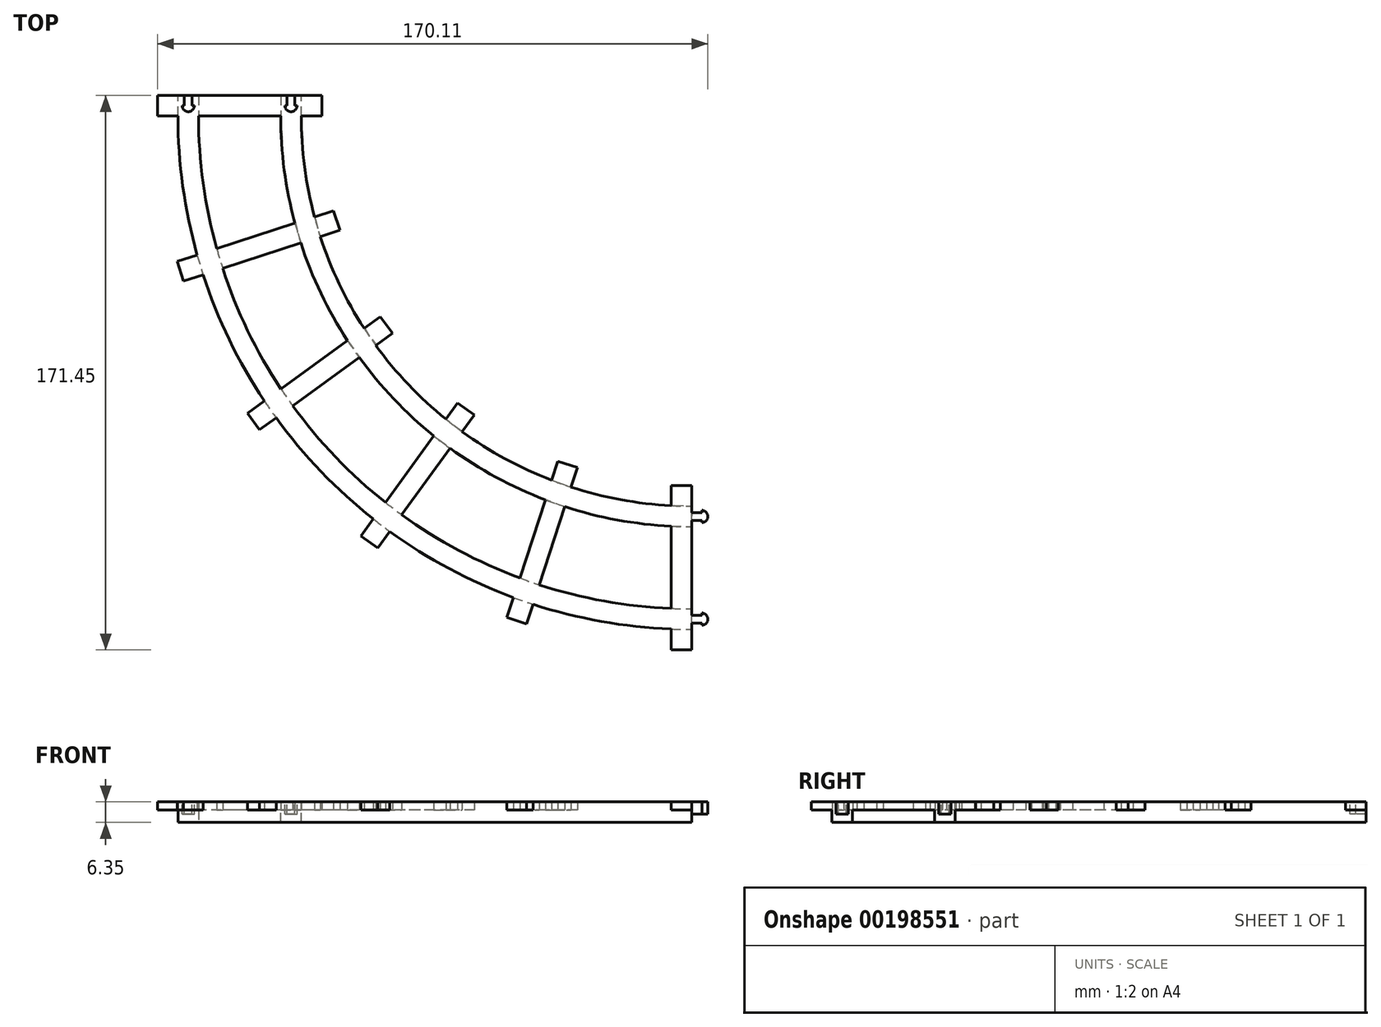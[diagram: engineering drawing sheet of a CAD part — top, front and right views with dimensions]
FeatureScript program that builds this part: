
annotation { "Feature Type Name" : "Feature", "Feature Type Description" : "" }
export const myFeature = defineFeature(function(context is Context, id is Id, definition is map)
    precondition{}
    {
        {
            var Q0;
            Q0=qCreatedBy(makeId("Top.planeOp"),FACE);
            var sketch = newSketch(context, id + "F0", { "sketchPlane" : qUnion([Q0])});
            skLineSegment(sketch, "E0.bottom", {"start": v(76.2, 76.2) * mm, "end": v(-76.2, 76.2) * mm, "construction": true});
            skPoint(sketch, "E0.middle", {"position": v(0, 0) * mm});
            skLineSegment(sketch, "E1", {"start": v(-76.2, 76.2) * mm, "end": v(-76.2, 101.6) * mm, "construction": true});
            skLineSegment(sketch, "E2", {"start": v(76.2, -76.2) * mm, "end": v(101.6, -76.2) * mm, "construction": true});
            skArc(sketch, "E3", {"start": v(76.2, -76.2) * mm, "mid": v(-31.56, -31.56) * mm, "end": v(-76.2, 76.2) * mm});
            skLineSegment(sketch, "E4", {"start": v(-76.2, 76.2) * mm, "end": v(-50.8, 76.2) * mm, "construction": true});
            skLineSegment(sketch, "E5", {"start": v(-50.8, 76.2) * mm, "end": v(-50.8, 101.6) * mm, "construction": true});
            skLineSegment(sketch, "E6", {"start": v(76.2, -76.2) * mm, "end": v(76.2, -50.8) * mm, "construction": true});
            skLineSegment(sketch, "E7", {"start": v(76.2, -50.8) * mm, "end": v(101.6, -50.8) * mm, "construction": true});
            skArc(sketch, "E8", {"start": v(76.2, -50.8) * mm, "mid": v(-13.6, -13.6) * mm, "end": v(-50.8, 76.2) * mm});
            skLineSegment(sketch, "E9", {"start": v(-76.2, 76.2) * mm, "end": v(-82.55, 76.2) * mm, "construction": true});
            skLineSegment(sketch, "E10", {"start": v(76.2, -76.2) * mm, "end": v(76.2, -82.55) * mm, "construction": true});
            skLineSegment(sketch, "E11", {"start": v(76.2, -82.55) * mm, "end": v(101.6, -82.55) * mm, "construction": true});
            skArc(sketch, "E12", {"start": v(76.2, -82.55) * mm, "mid": v(-36.05, -36.05) * mm, "end": v(-82.55, 76.2) * mm});
            skLineSegment(sketch, "E13", {"start": v(-82.55, 76.2) * mm, "end": v(-76.2, 76.2) * mm});
            skLineSegment(sketch, "E14", {"start": v(76.2, -82.55) * mm, "end": v(76.2, -76.2) * mm});
            skLineSegment(sketch, "E15", {"start": v(-50.8, 76.2) * mm, "end": v(-44.45, 76.2) * mm});
            skLineSegment(sketch, "E16", {"start": v(-44.45, 76.2) * mm, "end": v(-44.45, 101.6) * mm, "construction": true});
            skLineSegment(sketch, "E17", {"start": v(76.2, -44.45) * mm, "end": v(101.6, -44.45) * mm, "construction": true});
            skArc(sketch, "E18", {"start": v(76.2, -44.45) * mm, "mid": v(-9.11, -9.11) * mm, "end": v(-44.45, 76.2) * mm});
            skLineSegment(sketch, "E19", {"start": v(76.2, -44.45) * mm, "end": v(76.2, -50.8) * mm});
            skSolve(sketch);
        }
        {
            var Q0;
            Q0=qSketchRegion(id+"F0",true);
            extrude(context, id + "F1", {"entities" : qUnion([Q0]), "depth" : 6.35 * mm});
        }
        {
            var Q0;
            Q0=qCreatedBy(makeId("Top.planeOp"),FACE);
            var sketch = newSketch(context, id + "F2", { "sketchPlane" : qUnion([Q0])});
            skLineSegment(sketch, "E20.bottom", {"start": v(76.2, 76.2) * mm, "end": v(-76.2, 76.2) * mm, "construction": true});
            skLineSegment(sketch, "E20.top", {"start": v(76.2, -76.2) * mm, "end": v(-76.2, -76.2) * mm, "construction": true});
            skLineSegment(sketch, "E20.right", {"start": v(-76.2, 76.2) * mm, "end": v(-76.2, -76.2) * mm, "construction": true});
            skPoint(sketch, "E20.middle", {"position": v(0, 0) * mm});
            skLineSegment(sketch, "E21", {"start": v(76.2, -76.2) * mm, "end": v(76.2, -88.9) * mm, "construction": true});
            skLineSegment(sketch, "E22", {"start": v(76.2, -76.2) * mm, "end": v(76.2, -38.1) * mm, "construction": true});
            skLineSegment(sketch, "E23", {"start": v(76.2, -38.1) * mm, "end": v(69.85, -38.1) * mm});
            skLineSegment(sketch, "E24", {"start": v(76.2, -88.9) * mm, "end": v(69.85, -88.9) * mm});
            skLineSegment(sketch, "E25", {"start": v(69.85, -38.1) * mm, "end": v(69.85, -88.9) * mm});
            skLineSegment(sketch, "E26", {"start": v(76.2, -38.1) * mm, "end": v(76.2, -88.9) * mm});
            skArc(sketch, "E27.0", {"start": v(76.2, -44.45) * mm, "mid": v(-9.11, -9.11) * mm, "end": v(-44.45, 76.2) * mm, "construction": true});
            skLineSegment(sketch, "E28.1.0", {"start": v(40.88, -32.5) * mm, "end": v(25.18, -80.82) * mm});
            skLineSegment(sketch, "E28.1.1", {"start": v(34.84, -30.54) * mm, "end": v(19.14, -78.86) * mm});
            skLineSegment(sketch, "E28.1.2", {"start": v(40.88, -32.5) * mm, "end": v(34.84, -30.54) * mm});
            skLineSegment(sketch, "E28.1.3", {"start": v(25.18, -80.82) * mm, "end": v(19.14, -78.86) * mm});
            skLineSegment(sketch, "E28.2.0", {"start": v(9.02, -16.27) * mm, "end": v(-20.84, -57.37) * mm});
            skLineSegment(sketch, "E28.2.1", {"start": v(3.88, -12.54) * mm, "end": v(-25.98, -53.64) * mm});
            skLineSegment(sketch, "E28.2.2", {"start": v(9.02, -16.27) * mm, "end": v(3.88, -12.54) * mm});
            skLineSegment(sketch, "E28.2.3", {"start": v(-20.84, -57.37) * mm, "end": v(-25.98, -53.64) * mm});
            skLineSegment(sketch, "E28.3.0", {"start": v(-16.27, 9.02) * mm, "end": v(-57.37, -20.84) * mm});
            skLineSegment(sketch, "E28.3.1", {"start": v(-20, 14.15) * mm, "end": v(-61.1, -15.7) * mm});
            skLineSegment(sketch, "E28.3.2", {"start": v(-16.27, 9.02) * mm, "end": v(-20, 14.15) * mm});
            skLineSegment(sketch, "E28.3.3", {"start": v(-57.37, -20.84) * mm, "end": v(-61.1, -15.7) * mm});
            skLineSegment(sketch, "E28.4.0", {"start": v(-32.5, 40.88) * mm, "end": v(-80.82, 25.18) * mm});
            skLineSegment(sketch, "E28.4.1", {"start": v(-34.47, 46.92) * mm, "end": v(-82.78, 31.22) * mm});
            skLineSegment(sketch, "E28.4.2", {"start": v(-32.5, 40.88) * mm, "end": v(-34.47, 46.92) * mm});
            skLineSegment(sketch, "E28.4.3", {"start": v(-80.82, 25.18) * mm, "end": v(-82.78, 31.22) * mm});
            skLineSegment(sketch, "E28.5.0", {"start": v(-38.1, 76.2) * mm, "end": v(-88.9, 76.2) * mm});
            skLineSegment(sketch, "E28.5.1", {"start": v(-38.1, 82.55) * mm, "end": v(-88.9, 82.55) * mm});
            skLineSegment(sketch, "E28.5.2", {"start": v(-38.1, 76.2) * mm, "end": v(-38.1, 82.55) * mm});
            skLineSegment(sketch, "E28.5.3", {"start": v(-88.9, 76.2) * mm, "end": v(-88.9, 82.55) * mm});
            skLineSegment(sketch, "E28.anchor1", {"start": v(76.2, 76.2) * mm, "end": v(76.2, -88.9) * mm, "construction": true});
            skLineSegment(sketch, "E28.anchor2", {"start": v(76.2, 76.2) * mm, "end": v(-88.9, 76.2) * mm, "construction": true});
            skSolve(sketch);
        }
        {
            var Q0;
            Q0 = qSketchRegion(id + "F2", true);
            extrude(context, id + "F3", {"entities" : qUnion([Q0]), "operationType" : NewBodyOperationType.ADD, "depth" : 6.35 * mm, "hasSecondDirection" : true, "secondDirectionOppositeDirection" : false, "secondDirectionDepth" : 3.8 * mm});
        }
        {
            var Q0;
            Q0=makeQuery(id+"F3.opExtrude","CAP_FACE",FACE,{"disambiguationData":[OSD([sQuery(id+"F2.wireOp",EDGE,"E28.5.0"),sQuery(id+"F2.wireOp",EDGE,"E28.5.1"),sQuery(id+"F2.wireOp",EDGE,"E28.5.2"),sQuery(id+"F2.wireOp",EDGE,"E28.5.3")])],"isStart":true});
            var sketch = newSketch(context, id + "F4", { "sketchPlane" : qUnion([Q0])});
            skArc(sketch, "E29.0", {"start": v(76.2, 44.45) * mm, "mid": v(-9.11, 9.11) * mm, "end": v(-44.45, -76.2) * mm});
            skArc(sketch, "E30.0", {"start": v(76.2, 82.55) * mm, "mid": v(-36.05, 36.05) * mm, "end": v(-82.55, -76.2) * mm});
            skLineSegment(sketch, "E31", {"start": v(-82.55, -76.2) * mm, "end": v(-82.55, -82.55) * mm});
            skLineSegment(sketch, "E32", {"start": v(-44.45, -76.2) * mm, "end": v(-44.45, -82.55) * mm});
            skLineSegment(sketch, "E33", {"start": v(-44.45, -82.55) * mm, "end": v(-50.8, -82.55) * mm});
            skPoint(sketch, "E33.endSnap0", {"position": v(-63.5, -82.55) * mm});
            skLineSegment(sketch, "E34", {"start": v(-82.55, -82.55) * mm, "end": v(-76.2, -82.55) * mm});
            skLineSegment(sketch, "E35", {"start": v(-50.8, -82.55) * mm, "end": v(-50.8, -76.2) * mm});
            skLineSegment(sketch, "E36", {"start": v(-50.8, -76.2) * mm, "end": v(-44.45, -76.2) * mm});
            skLineSegment(sketch, "E37", {"start": v(-76.2, -82.55) * mm, "end": v(-76.2, -76.2) * mm});
            skLineSegment(sketch, "E38", {"start": v(-76.2, -76.2) * mm, "end": v(-82.55, -76.2) * mm});
            skSolve(sketch);
        }
        {
            var Q0;
            Q0 = qSketchRegion(id + "F4", true);
            var Q1;
            Q1=makeQuery(id+"F1.opExtrude","CAP_FACE",FACE,{"disambiguationData":[OSD([sQuery(id+"F0.wireOp",EDGE,"E8"),sQuery(id+"F0.wireOp",EDGE,"E15"),sQuery(id+"F0.wireOp",EDGE,"E18"),sQuery(id+"F0.wireOp",EDGE,"E19")])],"isStart":true});
            extrude(context, id + "F5", {"entities" : qUnion([Q0]), "operationType" : NewBodyOperationType.ADD, "endBound" : BoundingType.UP_TO_SURFACE, "endBoundEntityFace" : qUnion([Q1]), "depth" : 25.4 * mm});
        }
        {
            var Q0;
            Q0=makeQuery(id+"F3.boolean.opBoolean","MERGE",FACE,{"derivedFrom":[makeQuery(id+"F1.opExtrude","CAP_FACE",FACE,{"disambiguationData":[OSD([sQuery(id+"F0.wireOp",EDGE,"E3"),sQuery(id+"F0.wireOp",EDGE,"E12"),sQuery(id+"F0.wireOp",EDGE,"E13"),sQuery(id+"F0.wireOp",EDGE,"E14")])],"isStart":false}),makeQuery(id+"F1.opExtrude","CAP_FACE",FACE,{"disambiguationData":[OSD([sQuery(id+"F0.wireOp",EDGE,"E8"),sQuery(id+"F0.wireOp",EDGE,"E15"),sQuery(id+"F0.wireOp",EDGE,"E18"),sQuery(id+"F0.wireOp",EDGE,"E19")])],"isStart":false}),makeQuery(id+"F3.opExtrude","CAP_FACE",FACE,{"disambiguationData":[OSD([sQuery(id+"F2.wireOp",EDGE,"E23"),sQuery(id+"F2.wireOp",EDGE,"E24"),sQuery(id+"F2.wireOp",EDGE,"E25"),sQuery(id+"F2.wireOp",EDGE,"E26")])],"isStart":false}),makeQuery(id+"F3.opExtrude","CAP_FACE",FACE,{"disambiguationData":[OSD([sQuery(id+"F2.wireOp",EDGE,"E28.1.0"),sQuery(id+"F2.wireOp",EDGE,"E28.1.1"),sQuery(id+"F2.wireOp",EDGE,"E28.1.2"),sQuery(id+"F2.wireOp",EDGE,"E28.1.3")])],"isStart":false}),makeQuery(id+"F3.opExtrude","CAP_FACE",FACE,{"disambiguationData":[OSD([sQuery(id+"F2.wireOp",EDGE,"E28.2.0"),sQuery(id+"F2.wireOp",EDGE,"E28.2.1"),sQuery(id+"F2.wireOp",EDGE,"E28.2.2"),sQuery(id+"F2.wireOp",EDGE,"E28.2.3")])],"isStart":false}),makeQuery(id+"F3.opExtrude","CAP_FACE",FACE,{"disambiguationData":[OSD([sQuery(id+"F2.wireOp",EDGE,"E28.3.0"),sQuery(id+"F2.wireOp",EDGE,"E28.3.1"),sQuery(id+"F2.wireOp",EDGE,"E28.3.2"),sQuery(id+"F2.wireOp",EDGE,"E28.3.3")])],"isStart":false}),makeQuery(id+"F3.opExtrude","CAP_FACE",FACE,{"disambiguationData":[OSD([sQuery(id+"F2.wireOp",EDGE,"E28.4.0"),sQuery(id+"F2.wireOp",EDGE,"E28.4.1"),sQuery(id+"F2.wireOp",EDGE,"E28.4.2"),sQuery(id+"F2.wireOp",EDGE,"E28.4.3")])],"isStart":false}),makeQuery(id+"F3.opExtrude","CAP_FACE",FACE,{"disambiguationData":[OSD([sQuery(id+"F2.wireOp",EDGE,"E28.5.0"),sQuery(id+"F2.wireOp",EDGE,"E28.5.1"),sQuery(id+"F2.wireOp",EDGE,"E28.5.2"),sQuery(id+"F2.wireOp",EDGE,"E28.5.3")])],"isStart":false})]});
            var sketch = newSketch(context, id + "F6", { "sketchPlane" : qUnion([Q0])});
            skLineSegment(sketch, "E39", {"start": v(76.2, -47.62) * mm, "end": v(79.38, -47.62) * mm, "construction": true});
            skLineSegment(sketch, "E40", {"start": v(76.2, -47.62) * mm, "end": v(76.2, -46.43) * mm});
            skLineSegment(sketch, "E41.MirrorCS", {"start": v(76.2, -47.62) * mm, "end": v(76.2, -48.81) * mm});
            skLineSegment(sketch, "E42", {"start": v(76.2, -46.43) * mm, "end": v(79.38, -46.43) * mm});
            skLineSegment(sketch, "E43", {"start": v(79.38, -46.43) * mm, "end": v(79.38, -45.72) * mm});
            skLineSegment(sketch, "E44.MirrorCS", {"start": v(76.2, -48.81) * mm, "end": v(79.38, -48.81) * mm});
            skLineSegment(sketch, "E45.MirrorCS", {"start": v(79.38, -48.81) * mm, "end": v(79.38, -49.53) * mm});
            skArc(sketch, "E46", {"start": v(79.37, -49.53) * mm, "mid": v(81.21, -47.62) * mm, "end": v(79.37, -45.72) * mm});
            skLineSegment(sketch, "E47", {"start": v(76.2, -38.1) * mm, "end": v(76.2, -46.43) * mm, "construction": true});
            skLineSegment(sketch, "E48", {"start": v(76.2, -38.1) * mm, "end": v(76.2, -88.9) * mm, "construction": true});
            skPoint(sketch, "E49", {"position": v(76.2, -63.5) * mm});
            skLineSegment(sketch, "E50", {"start": v(76.2, -63.5) * mm, "end": v(127.23, -63.5) * mm, "construction": true});
            skLineSegment(sketch, "E51.MirrorCS", {"start": v(76.2, -79.38) * mm, "end": v(76.2, -80.57) * mm});
            skLineSegment(sketch, "E52.MirrorCS", {"start": v(76.2, -80.57) * mm, "end": v(79.38, -80.57) * mm});
            skLineSegment(sketch, "E53.MirrorCS", {"start": v(79.38, -80.57) * mm, "end": v(79.38, -81.28) * mm});
            skArc(sketch, "E54.MirrorCS", {"start": v(79.37, -77.47) * mm, "mid": v(81.21, -79.38) * mm, "end": v(79.37, -81.28) * mm});
            skLineSegment(sketch, "E55.MirrorCS", {"start": v(76.2, -79.38) * mm, "end": v(76.2, -78.19) * mm});
            skLineSegment(sketch, "E56.MirrorCS", {"start": v(76.2, -78.19) * mm, "end": v(79.38, -78.19) * mm});
            skLineSegment(sketch, "E57", {"start": v(79.38, -77.47) * mm, "end": v(79.38, -78.19) * mm});
            skSolve(sketch);
        }
        {
            var Q0;
            Q0 = qSketchRegion(id + "F6", true);
            extrude(context, id + "F7", {"entities" : qUnion([Q0]), "operationType" : NewBodyOperationType.ADD, "oppositeDirection" : true, "depth" : 3.8 * mm});
        }
        {
            var Q0;
            Q0=makeQuery(id+"F7.boolean.opBoolean","MERGE",FACE,{"derivedFrom":[makeQuery(id+"F3.boolean.opBoolean","MERGE",FACE,{"derivedFrom":[makeQuery(id+"F1.opExtrude","CAP_FACE",FACE,{"disambiguationData":[OSD([sQuery(id+"F0.wireOp",EDGE,"E3"),sQuery(id+"F0.wireOp",EDGE,"E12"),sQuery(id+"F0.wireOp",EDGE,"E13"),sQuery(id+"F0.wireOp",EDGE,"E14")])],"isStart":false}),makeQuery(id+"F1.opExtrude","CAP_FACE",FACE,{"disambiguationData":[OSD([sQuery(id+"F0.wireOp",EDGE,"E8"),sQuery(id+"F0.wireOp",EDGE,"E15"),sQuery(id+"F0.wireOp",EDGE,"E18"),sQuery(id+"F0.wireOp",EDGE,"E19")])],"isStart":false}),makeQuery(id+"F3.opExtrude","CAP_FACE",FACE,{"disambiguationData":[OSD([sQuery(id+"F2.wireOp",EDGE,"E23"),sQuery(id+"F2.wireOp",EDGE,"E24"),sQuery(id+"F2.wireOp",EDGE,"E25"),sQuery(id+"F2.wireOp",EDGE,"E26")])],"isStart":false}),makeQuery(id+"F3.opExtrude","CAP_FACE",FACE,{"disambiguationData":[OSD([sQuery(id+"F2.wireOp",EDGE,"E28.1.0"),sQuery(id+"F2.wireOp",EDGE,"E28.1.1"),sQuery(id+"F2.wireOp",EDGE,"E28.1.2"),sQuery(id+"F2.wireOp",EDGE,"E28.1.3")])],"isStart":false}),makeQuery(id+"F3.opExtrude","CAP_FACE",FACE,{"disambiguationData":[OSD([sQuery(id+"F2.wireOp",EDGE,"E28.2.0"),sQuery(id+"F2.wireOp",EDGE,"E28.2.1"),sQuery(id+"F2.wireOp",EDGE,"E28.2.2"),sQuery(id+"F2.wireOp",EDGE,"E28.2.3")])],"isStart":false}),makeQuery(id+"F3.opExtrude","CAP_FACE",FACE,{"disambiguationData":[OSD([sQuery(id+"F2.wireOp",EDGE,"E28.3.0"),sQuery(id+"F2.wireOp",EDGE,"E28.3.1"),sQuery(id+"F2.wireOp",EDGE,"E28.3.2"),sQuery(id+"F2.wireOp",EDGE,"E28.3.3")])],"isStart":false}),makeQuery(id+"F3.opExtrude","CAP_FACE",FACE,{"disambiguationData":[OSD([sQuery(id+"F2.wireOp",EDGE,"E28.4.0"),sQuery(id+"F2.wireOp",EDGE,"E28.4.1"),sQuery(id+"F2.wireOp",EDGE,"E28.4.2"),sQuery(id+"F2.wireOp",EDGE,"E28.4.3")])],"isStart":false}),makeQuery(id+"F3.opExtrude","CAP_FACE",FACE,{"disambiguationData":[OSD([sQuery(id+"F2.wireOp",EDGE,"E28.5.0"),sQuery(id+"F2.wireOp",EDGE,"E28.5.1"),sQuery(id+"F2.wireOp",EDGE,"E28.5.2"),sQuery(id+"F2.wireOp",EDGE,"E28.5.3")])],"isStart":false})]}),makeQuery(id+"F7.opExtrude","CAP_FACE",FACE,{"disambiguationData":[OSD([sQuery(id+"F6.wireOp",EDGE,"E40"),sQuery(id+"F6.wireOp",EDGE,"E41.MirrorCS"),sQuery(id+"F6.wireOp",EDGE,"E42"),sQuery(id+"F6.wireOp",EDGE,"E43"),sQuery(id+"F6.wireOp",EDGE,"E44.MirrorCS"),sQuery(id+"F6.wireOp",EDGE,"E45.MirrorCS"),sQuery(id+"F6.wireOp",EDGE,"E46")])],"isStart":true}),makeQuery(id+"F7.opExtrude","CAP_FACE",FACE,{"disambiguationData":[OSD([sQuery(id+"F6.wireOp",EDGE,"E51.MirrorCS"),sQuery(id+"F6.wireOp",EDGE,"E52.MirrorCS"),sQuery(id+"F6.wireOp",EDGE,"E54.MirrorCS"),sQuery(id+"F6.wireOp",EDGE,"E55.MirrorCS"),sQuery(id+"F6.wireOp",EDGE,"E56.MirrorCS"),sQuery(id+"F6.wireOp",EDGE,"E53.MirrorCS"),sQuery(id+"F6.wireOp",EDGE,"E57")])],"isStart":true})]});
            var sketch = newSketch(context, id + "F8", { "sketchPlane" : qUnion([Q0])});
            skLineSegment(sketch, "E58", {"start": v(-47.62, 82.55) * mm, "end": v(-47.62, 79.37) * mm, "construction": true});
            skLineSegment(sketch, "E59", {"start": v(-47.62, 82.55) * mm, "end": v(-46.43, 82.55) * mm});
            skLineSegment(sketch, "E60.MirrorCS", {"start": v(-47.62, 82.55) * mm, "end": v(-48.81, 82.55) * mm});
            skLineSegment(sketch, "E61", {"start": v(-46.43, 82.55) * mm, "end": v(-46.43, 79.37) * mm});
            skLineSegment(sketch, "E62", {"start": v(-46.43, 79.37) * mm, "end": v(-45.72, 79.37) * mm});
            skLineSegment(sketch, "E63.MirrorCS", {"start": v(-48.81, 82.55) * mm, "end": v(-48.81, 79.37) * mm});
            skLineSegment(sketch, "E64.MirrorCS", {"start": v(-48.81, 79.37) * mm, "end": v(-49.53, 79.37) * mm});
            skArc(sketch, "E65", {"start": v(-49.53, 79.37) * mm, "mid": v(-47.62, 77.54) * mm, "end": v(-45.72, 79.37) * mm});
            skLineSegment(sketch, "E66", {"start": v(-38.1, 82.55) * mm, "end": v(-46.43, 82.55) * mm, "construction": true});
            skLineSegment(sketch, "E67", {"start": v(-38.1, 82.55) * mm, "end": v(-88.9, 82.55) * mm, "construction": true});
            skLineSegment(sketch, "E68", {"start": v(-63.5, 82.55) * mm, "end": v(-63.5, 60.87) * mm, "construction": true});
            skLineSegment(sketch, "E69.MirrorCS", {"start": v(-79.38, 82.55) * mm, "end": v(-80.57, 82.55) * mm});
            skLineSegment(sketch, "E70.MirrorCS", {"start": v(-78.19, 79.37) * mm, "end": v(-77.47, 79.37) * mm});
            skLineSegment(sketch, "E71.MirrorCS", {"start": v(-80.57, 79.37) * mm, "end": v(-81.28, 79.37) * mm});
            skLineSegment(sketch, "E72.MirrorCS", {"start": v(-79.38, 82.55) * mm, "end": v(-78.19, 82.55) * mm});
            skArc(sketch, "E73.MirrorCS", {"start": v(-77.47, 79.37) * mm, "mid": v(-79.38, 77.54) * mm, "end": v(-81.28, 79.37) * mm});
            skLineSegment(sketch, "E74.MirrorCS", {"start": v(-78.19, 82.55) * mm, "end": v(-78.19, 79.37) * mm});
            skLineSegment(sketch, "E75.MirrorCS", {"start": v(-80.57, 82.55) * mm, "end": v(-80.57, 79.37) * mm});
            skLineSegment(sketch, "E76.MirrorCS", {"start": v(-79.38, 82.55) * mm, "end": v(-79.38, 79.37) * mm, "construction": true});
            skSolve(sketch);
        }
        {
            var Q0;
            Q0 = qSketchRegion(id + "F8", true);
            extrude(context, id + "F9", {"entities" : qUnion([Q0]), "operationType" : NewBodyOperationType.REMOVE, "oppositeDirection" : true, "depth" : 3.8 * mm});
        }
    });
